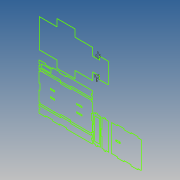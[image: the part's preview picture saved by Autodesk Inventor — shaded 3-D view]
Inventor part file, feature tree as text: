
AUTODESK INVENTOR PART (.ipt)
format: ipt  version: 2020 (Build 240168000, 168)  size: 146,944 bytes
history: native  units: mm
features: sketch x1
ambient origin geometry x8: Origin, YZ Plane, XZ Plane, XY Plane, X Axis, Y Axis, Z Axis, Center Point
feature tree (1):
  sketch  "Sketch1"  dims[d303=0.5mm d304=0.5mm]
